# Revit family: FU_Stool_Sandler_Viki 4-15
name_source: partatom
category: Furniture
units: mm (PartAtom-declared; Revit-internal decimal feet)

## family parameters
Always vertical = Yes
Cut with Voids When Loaded = No
OmniClass Number = 23.40.20.00
OmniClass Title = General Furniture and Specialties
Render Appearance Source = Family Geometry
Room Calculation Point = No
Shared = No
Work Plane-Based = No

## types (1)
- Viki 4.15
    Default Elevation = 0 mm  [stored 0 ft]
    Depth = 500 mm  [stored 1.64042 ft]
    Description = Counter stool with wooden seat on a solid beech frame with stretchers. Produced to custom height per customer specification, from 23.5”-29” seat height
    Height = 770 mm  [stored 2.52625 ft]
    Manufacturer = Sandler
    Model = Viki 4.15
    URL = https://www.sandlerseating.com
    Width = 490 mm  [stored 1.60761 ft]

note: [stored X ft] marks values corroborated as IEEE doubles in the binary element streams (Revit-internal decimal feet)

## geometry (parser evidence)
native form markers: Sweep x5
no freeform markers — native parametric forms only
